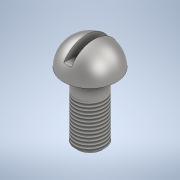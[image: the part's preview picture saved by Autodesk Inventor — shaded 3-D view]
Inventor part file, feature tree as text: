
AUTODESK INVENTOR PART (.ipt)
format: ipt  version: 2021 (Build 250183000, 183)  size: 137,216 bytes
history: native  units: mm
features: other x3, sketch x2, thread x1, chamfer x1, extrude x1
ambient origin geometry x8: Origin, YZ Plane, XZ Plane, XY Plane, X Axis, Y Axis, Z Axis, Center Point
bodies: Body1 (feature_tree)
feature tree (8):
  other  "Sólido1"
  other  "Revolução1"
  thread  "Rosca1"  [1 undecoded]
  chamfer  "Chanfro1"  Angle=90.0deg  [1 undecoded]
  other  "Plano de trabalho1"
  extrude  "Extrusão1"  Depth=2.0mm TaperAngle=0.0deg
  sketch  "Esboço1"  dims[d1=2.25mm]
  sketch  "Esboço2"  dims[d2=10.0mm d3=90.0deg d4=7.0mm d5=0.0mm d6=0.4mm d7=2.0mm d8=45.0deg d9=4.0mm d10=1.2mm d11=2.0mm d12=0.0mm]
note: 2 required parameter values undecoded (feature->parameter linkage not recoverable at this tier; creation-order binding heuristic only, values carry confidence <= 0.55)
